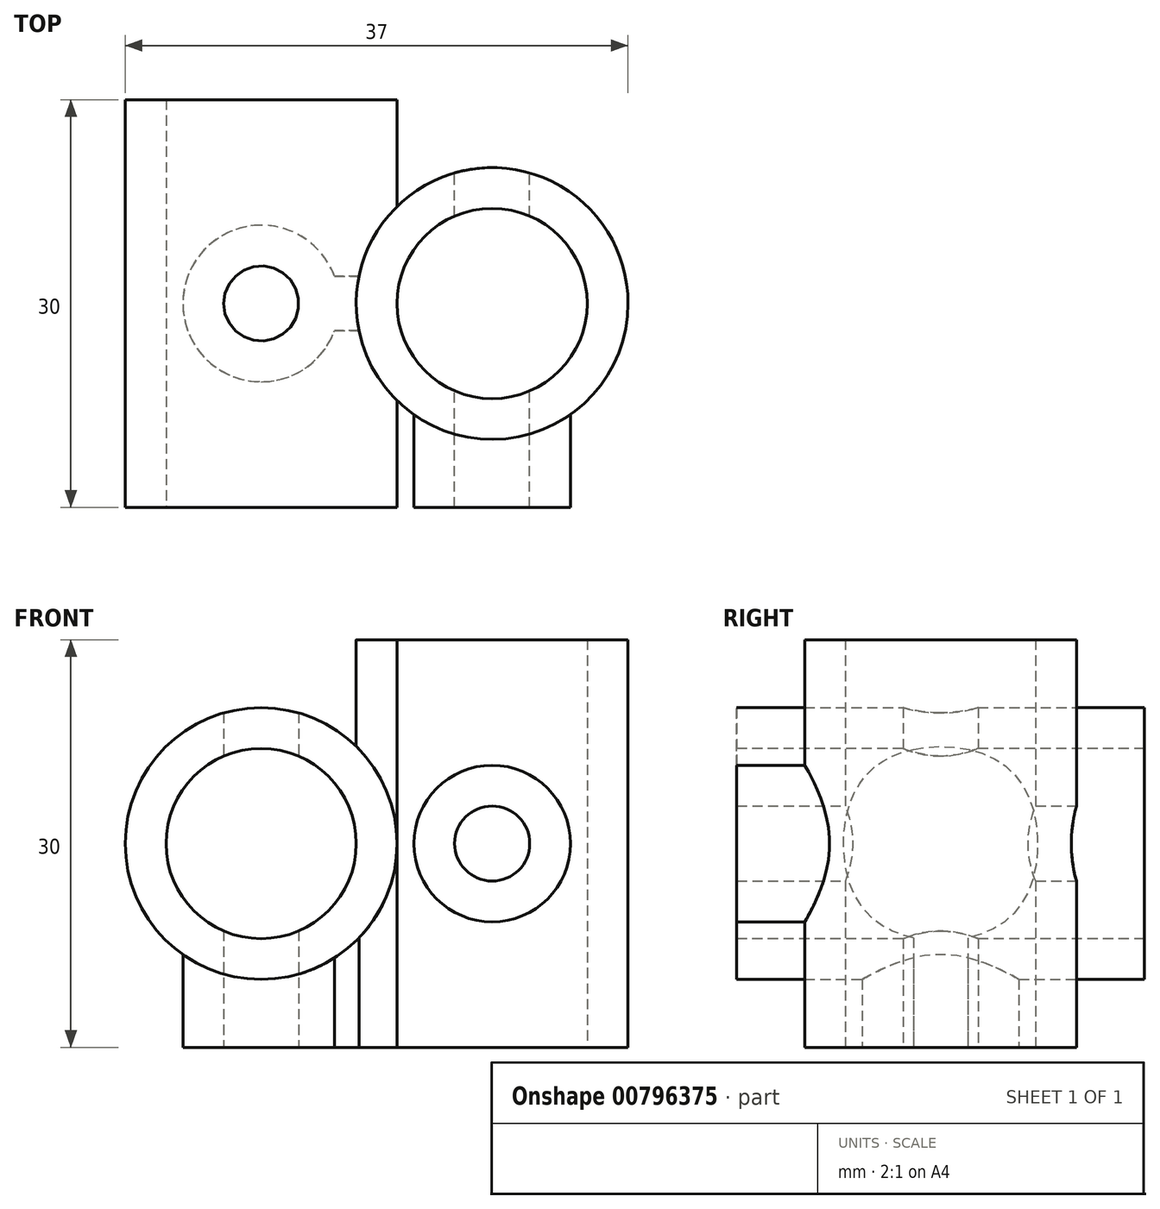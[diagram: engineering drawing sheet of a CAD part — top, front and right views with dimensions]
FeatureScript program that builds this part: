
annotation { "Feature Type Name" : "Feature", "Feature Type Description" : "" }
export const myFeature = defineFeature(function(context is Context, id is Id, definition is map)
    precondition{}
    {
        {
            var Q0;
            Q0=qCreatedBy(makeId("Right.planeOp"),FACE);
            cPlane(context, id + "F0", {"entities" : qUnion([Q0]), "cplaneType" : CPlaneType.OFFSET, "offset" : 17 * mm, "oppositeDirection" : true, "width" : 150 * mm, "height" : 150 * mm});
        }
        {
            var Q0;
            Q0=qCreatedBy(makeId("Top.planeOp"),FACE);
            var sketch = newSketch(context, id + "F1", { "sketchPlane" : qUnion([Q0])});
            skArc(sketch, "E0", {"start": v(-9.8, -2) * mm, "mid": v(10, 0) * mm, "end": v(-9.8, 2) * mm});
            skArc(sketch, "E1", {"start": v(-11.6, 2) * mm, "mid": v(-22.76, 0) * mm, "end": v(-11.6, -2) * mm});
            skLineSegment(sketch, "E2", {"start": v(-11.6, 2) * mm, "end": v(-9.8, 2) * mm});
            skLineSegment(sketch, "E3", {"start": v(-11.6, -2) * mm, "end": v(-9.8, -2) * mm});
            skSolve(sketch);
        }
        {
            var Q0;
            Q0=makeQuery(id+"F1.imprint","IMPRINT",FACE,{"disambiguationData":[TD([[makeQuery(id+"F1.imprint","IMPRINT",EDGE,{"derivedFrom":sQuery(id+"F1.wireOp",EDGE,"E0")}),1.0]])]});
            var Q1;
            Q1=makeQuery(id+"F1.imprint","IMPRINT",FACE,{"disambiguationData":[TD([[makeQuery(id+"F1.imprint","IMPRINT",EDGE,{"derivedFrom":sQuery(id+"F1.wireOp",EDGE,"wlYGbSdg-z0a7-mfQQ-gPmd-itWBD6KfdEBn")}),1.0]])]});
            extrude(context, id + "F2", {"entities" : qUnion([Q0, Q1]), "endBound" : BoundingType.SYMMETRIC, "depth" : 30 * mm, "offsetDistance" : 25 * mm});
        }
        {
            var Q0;
            Q0=qCreatedBy(makeId("Front.planeOp"),FACE);
            var sketch = newSketch(context, id + "F3", { "sketchPlane" : qUnion([Q0])});
            skCircle(sketch, "E4", {"center": v(-17, 0) * mm, "radius": 10 * mm});
            skCircle(sketch, "E5", {"center": v(0, 0) * mm, "radius": 5.76 * mm});
            skSolve(sketch);
        }
        {
            var Q0;
            Q0 = qSketchRegion(id + "F3", true);
            extrude(context, id + "F4", {"entities" : qUnion([Q0]), "operationType" : NewBodyOperationType.ADD, "endBound" : BoundingType.SYMMETRIC, "depth" : 30 * mm, "offsetDistance" : 25 * mm});
        }
        {
            var Q0;
            Q0=makeQuery(id+"F4.opExtrude","CAP_FACE",FACE,{"disambiguationData":[OSD([sQuery(id+"F3.wireOp",EDGE,"E4")])],"isStart":false});
            var Q1;
            Q1=makeQuery(id+"F4.opExtrude","CAP_FACE",FACE,{"disambiguationData":[OSD([sQuery(id+"F3.wireOp",EDGE,"E5")])],"isStart":false});
            var Q2;
            Q2=makeQuery(id+"F2.opExtrude","CAP_FACE",FACE,{"disambiguationData":[OSD([sQuery(id+"F1.wireOp",EDGE,"E0"),sQuery(id+"F1.wireOp",EDGE,"E1"),sQuery(id+"F1.wireOp",EDGE,"E2"),sQuery(id+"F1.wireOp",EDGE,"E3")])],"isStart":true});
            var Q3;
            Q3=makeQuery(id+"F4.opExtrude","CAP_FACE",FACE,{"disambiguationData":[OSD([sQuery(id+"F3.wireOp",EDGE,"E4")])],"isStart":true});
            var Q4;
            Q4=makeQuery(id+"F4.opExtrude","CAP_FACE",FACE,{"disambiguationData":[OSD([sQuery(id+"F3.wireOp",EDGE,"E5")])],"isStart":true});
            var Q5;
            Q5=makeQuery(id+"F2.opExtrude","CAP_FACE",FACE,{"disambiguationData":[OSD([sQuery(id+"F1.wireOp",EDGE,"E0"),sQuery(id+"F1.wireOp",EDGE,"E1"),sQuery(id+"F1.wireOp",EDGE,"E2"),sQuery(id+"F1.wireOp",EDGE,"E3")])],"isStart":false});
            shell(context, id + "F5", {"entities" : qUnion([Q0, Q1, Q2, Q3, Q4, Q5]), "thickness" : 3 * mm});
        }
        {
            var Q0;
            Q0=makeQuery(id+"F4.opExtrude","CAP_FACE",FACE,{"disambiguationData":[OSD([sQuery(id+"F3.wireOp",EDGE,"E4")])],"isStart":false});
            var sketch = newSketch(context, id + "F6", { "sketchPlane" : qUnion([Q0])});
            skCircle(sketch, "E6", {"center": v(-17, 0) * mm, "radius": 7 * mm});
            skSolve(sketch);
        }
        {
            var Q0;
            Q0 = qSketchRegion(id + "F6", true);
            extrude(context, id + "F7", {"entities" : qUnion([Q0]), "operationType" : NewBodyOperationType.REMOVE, "endBound" : BoundingType.THROUGH_ALL, "oppositeDirection" : true, "depth" : 25 * mm, "offsetDistance" : 25 * mm});
        }
        {
            var Q0;
            Q0=makeQuery(id+"F2.opExtrude","CAP_FACE",FACE,{"disambiguationData":[OSD([sQuery(id+"F1.wireOp",EDGE,"E0"),sQuery(id+"F1.wireOp",EDGE,"E1"),sQuery(id+"F1.wireOp",EDGE,"E2"),sQuery(id+"F1.wireOp",EDGE,"E3")])],"isStart":true});
            var sketch = newSketch(context, id + "F8", { "sketchPlane" : qUnion([Q0])});
            skCircle(sketch, "E7", {"center": v(-17, 0) * mm, "radius": 2.76 * mm});
            skSolve(sketch);
        }
        {
            var Q0;
            Q0 = qSketchRegion(id + "F8", true);
            extrude(context, id + "F9", {"entities" : qUnion([Q0]), "operationType" : NewBodyOperationType.REMOVE, "endBound" : BoundingType.THROUGH_ALL, "oppositeDirection" : true, "depth" : 25 * mm, "offsetDistance" : 25 * mm});
        }
        {
            var Q0;
            Q0=makeQuery(id+"F2.opExtrude","CAP_FACE",FACE,{"disambiguationData":[OSD([sQuery(id+"F1.wireOp",EDGE,"E0"),sQuery(id+"F1.wireOp",EDGE,"E1"),sQuery(id+"F1.wireOp",EDGE,"E2"),sQuery(id+"F1.wireOp",EDGE,"E3")])],"isStart":false});
            var sketch = newSketch(context, id + "F10", { "sketchPlane" : qUnion([Q0])});
            skArc(sketch, "E8", {"start": v(-9.8, -2) * mm, "mid": v(-10, 0) * mm, "end": v(-9.8, 2) * mm});
            skLineSegment(sketch, "E9.0", {"start": v(-11.6, 2) * mm, "end": v(-9.8, 2) * mm});
            skArc(sketch, "E10.0", {"start": v(-11.6, 2) * mm, "mid": v(-22.76, 0) * mm, "end": v(-11.6, -2) * mm});
            skLineSegment(sketch, "E11.0", {"start": v(-11.6, -2) * mm, "end": v(-9.8, -2) * mm});
            skSolve(sketch);
        }
        {
            var Q0;
            Q0 = qSketchRegion(id + "F10", true);
            var Q1;
            Q1=makeQuery(id+"F4.opExtrude","SWEPT_FACE",FACE,{"disambiguationData":[OSD([sQuery(id+"F3.wireOp",EDGE,"E4")])]});
            extrude(context, id + "F11", {"entities" : qUnion([Q0]), "operationType" : NewBodyOperationType.REMOVE, "endBound" : BoundingType.UP_TO_SURFACE, "oppositeDirection" : true, "depth" : 25 * mm, "endBoundEntityFace" : qUnion([Q1]), "offsetDistance" : 25 * mm});
        }
        {
            var Q0;
            Q0=makeQuery(id+"F2.opExtrude","CAP_FACE",FACE,{"disambiguationData":[OSD([sQuery(id+"F1.wireOp",EDGE,"E0"),sQuery(id+"F1.wireOp",EDGE,"E1"),sQuery(id+"F1.wireOp",EDGE,"E2"),sQuery(id+"F1.wireOp",EDGE,"E3")])],"isStart":false});
            var sketch = newSketch(context, id + "F12", { "sketchPlane" : qUnion([Q0])});
            skLineSegment(sketch, "E12", {"start": v(-5.76, 8.17) * mm, "end": v(-5.76, 15) * mm});
            skLineSegment(sketch, "E13.0", {"start": v(5.76, 15) * mm, "end": v(-5.76, 15) * mm});
            skLineSegment(sketch, "E14", {"start": v(5.76, 15) * mm, "end": v(5.76, 8.17) * mm});
            skArc(sketch, "E15.0", {"start": v(5.76, 8.17) * mm, "mid": v(0, 10) * mm, "end": v(-5.76, 8.17) * mm});
            skSolve(sketch);
        }
        {
            var Q0;
            Q0 = qSketchRegion(id + "F12", true);
            extrude(context, id + "F13", {"entities" : qUnion([Q0]), "operationType" : NewBodyOperationType.REMOVE, "oppositeDirection" : true, "depth" : 25 * mm, "offsetDistance" : 25 * mm});
        }
    });
